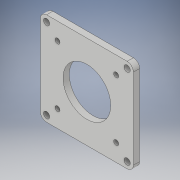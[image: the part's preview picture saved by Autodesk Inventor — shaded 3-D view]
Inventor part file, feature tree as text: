
AUTODESK INVENTOR PART (.ipt)
format: ipt  version: 2019.3 (Build 233278000, 278)  size: 148,992 bytes
history: native  units: mm
features: extrude x1, fillet x1, sketch x1
ambient origin geometry x8: Origin, YZ Plane, XZ Plane, XY Plane, X Axis, Y Axis, Z Axis, Center Point
bodies: Solid1 (feature_tree)
feature tree (3):
  extrude  "Extrusion1"  Depth=5.0mm
  fillet  "Fillet1"  Radius=4.0mm
  sketch  "Sketch1"  dims[d0=4.0mm d1=4.0mm d2=4.0mm d3=4.0mm d4=38.2mm d5=47.0mm d6=47.0mm d7=47.0mm d8=47.0mm d9=23.5mm d10=23.5mm d11=23.5mm d12=23.5mm d13=74.5mm d14=74.5mm d15=37.25mm d16=37.25mm d17=5.0mm d18=5.0mm d19=5.0mm d20=5.0mm d21=64.5mm d22=64.5mm d23=64.5mm d24=64.5mm d25=5.0mm d26=5.0mm d27=5.0mm d28=5.0mm d29=5.0mm d30=0.0mm d31=5.0mm]
